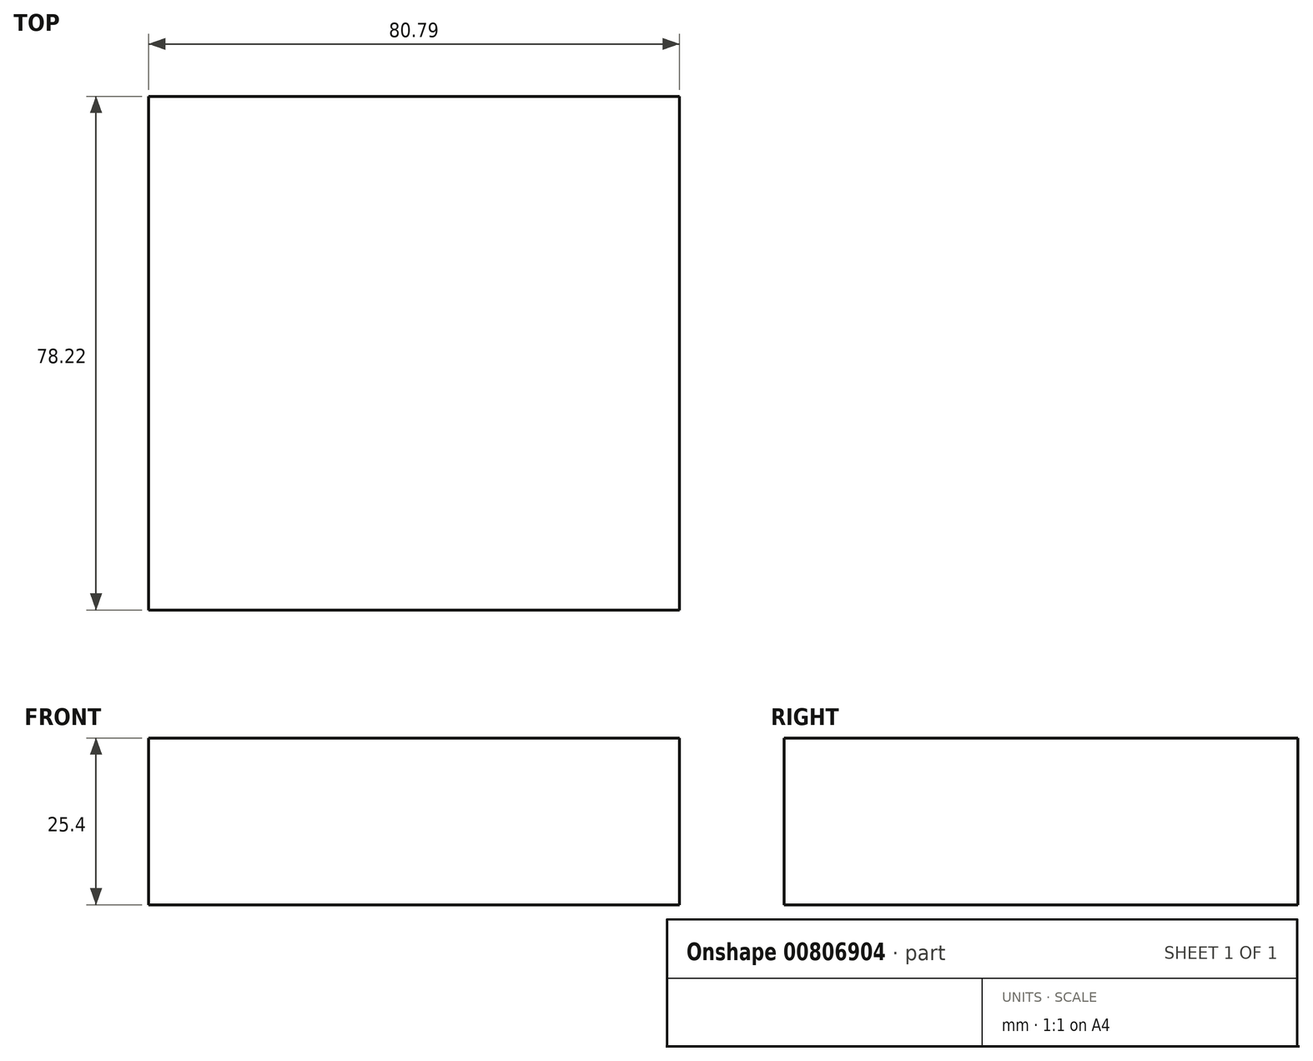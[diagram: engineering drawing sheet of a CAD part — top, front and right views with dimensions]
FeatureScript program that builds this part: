
annotation { "Feature Type Name" : "Feature", "Feature Type Description" : "" }
export const myFeature = defineFeature(function(context is Context, id is Id, definition is map)
    precondition{}
    {
        {
            var Q0;
            Q0=qCreatedBy(makeId("Top.planeOp"),FACE);
            var sketch = newSketch(context, id + "F0", { "sketchPlane" : qUnion([Q0])});
            skLineSegment(sketch, "E0.bottom", {"start": v(41.14, -31) * mm, "end": v(-39.65, -31) * mm});
            skLineSegment(sketch, "E0.top", {"start": v(41.14, 47.23) * mm, "end": v(-39.65, 47.23) * mm});
            skLineSegment(sketch, "E0.left", {"start": v(41.14, -31) * mm, "end": v(41.14, 47.23) * mm});
            skLineSegment(sketch, "E0.right", {"start": v(-39.65, -31) * mm, "end": v(-39.65, 47.23) * mm});
            skSolve(sketch);
        }
        {
            var Q0;
            Q0 = qSketchRegion(id + "F0", true);
            extrude(context, id + "F1", {"entities" : qUnion([Q0]), "depth" : 25.4 * mm, "offsetDistance" : 25.4 * mm});
        }
    });
